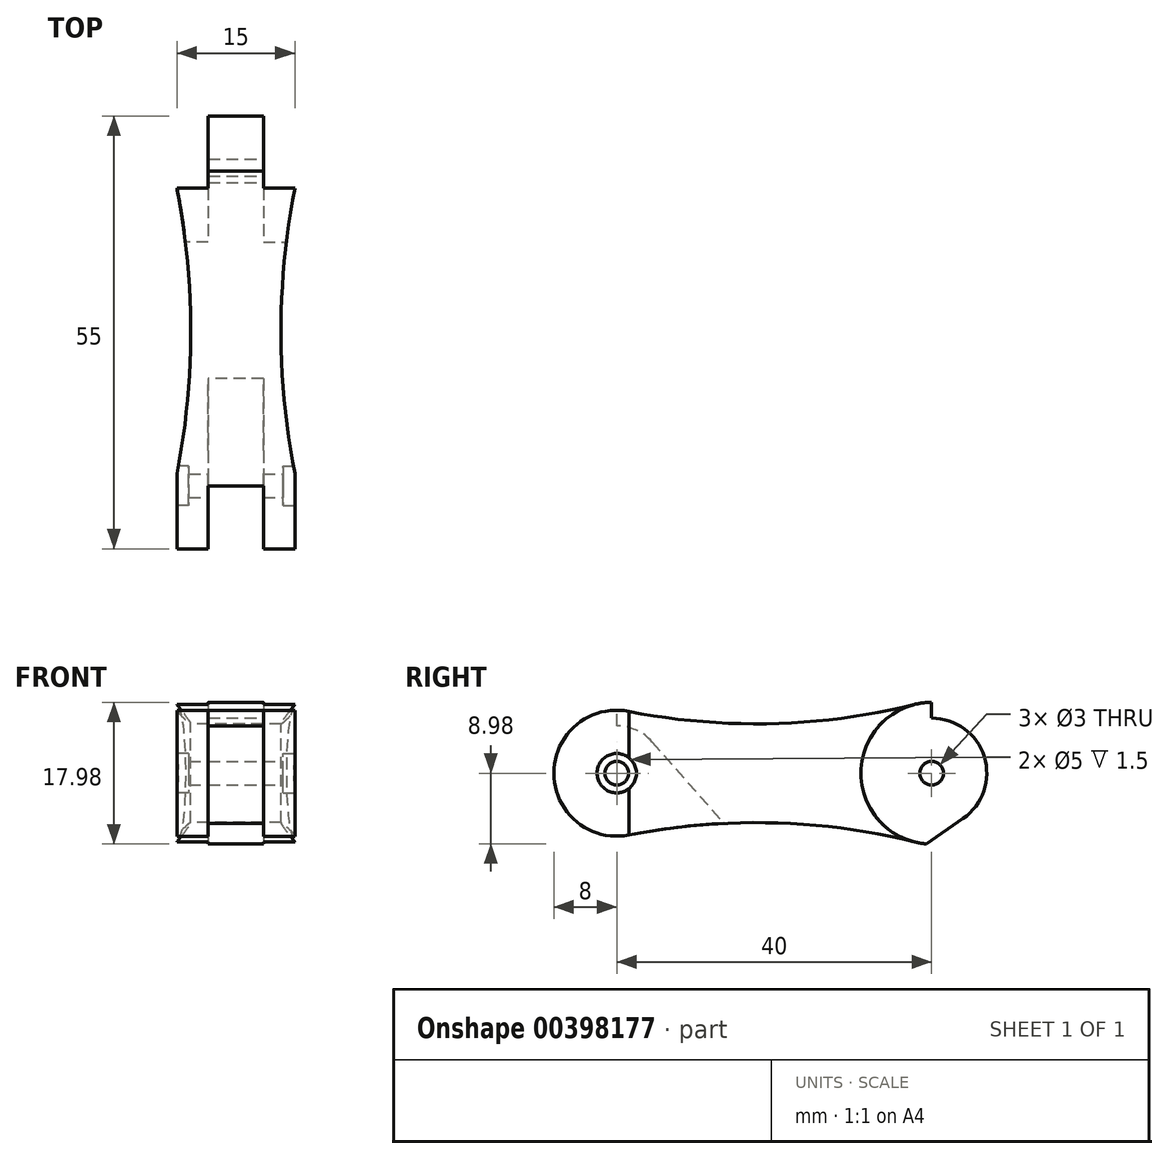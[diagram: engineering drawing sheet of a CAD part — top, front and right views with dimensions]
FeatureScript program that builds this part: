
annotation { "Feature Type Name" : "Feature", "Feature Type Description" : "" }
export const myFeature = defineFeature(function(context is Context, id is Id, definition is map)
    precondition{}
    {
        {
            var Q0;
            Q0=qCreatedBy(makeId("Right.planeOp"),FACE);
            var sketch = newSketch(context, id + "F0", { "sketchPlane" : qUnion([Q0])});
            skArc(sketch, "E0", {"start": v(1.54, 7.85) * mm, "mid": v(-8, 0) * mm, "end": v(1.54, -7.85) * mm});
            skLineSegment(sketch, "E1", {"start": v(-29.92, 0) * mm, "end": v(87.26, 0) * mm, "construction": true});
            skArc(sketch, "E2", {"start": v(37.83, -8.74) * mm, "mid": v(49, 0) * mm, "end": v(37.83, 8.74) * mm});
            skArc(sketch, "E3", {"start": v(1.54, 7.85) * mm, "mid": v(19.74, 6.3) * mm, "end": v(37.83, 8.74) * mm});
            skArc(sketch, "E4", {"start": v(37.83, -8.74) * mm, "mid": v(19.74, -6.3) * mm, "end": v(1.54, -7.85) * mm});
            skSolve(sketch);
        }
        {
            var Q0;
            Q0=qSketchRegion(id+"F0",true);
            extrude(context, id + "F1", {"entities" : qUnion([Q0]), "depth" : 4 * mm});
        }
        {
            var Q0;
            Q0=makeQuery(id+"F1.opExtrude","CAP_FACE",FACE,{"disambiguationData":[OSD([sQuery(id+"F0.wireOp",EDGE,"E0"),sQuery(id+"F0.wireOp",EDGE,"E2"),sQuery(id+"F0.wireOp",EDGE,"E3"),sQuery(id+"F0.wireOp",EDGE,"E4")])],"isStart":false});
            var sketch = newSketch(context, id + "F2", { "sketchPlane" : qUnion([Q0])});
            skArc(sketch, "E5.0", {"start": v(37.83, -8.74) * mm, "mid": v(49, 0) * mm, "end": v(37.83, 8.74) * mm});
            skLineSegment(sketch, "E6", {"start": v(0, 0) * mm, "end": v(34.9, 0) * mm, "construction": true});
            skArc(sketch, "E7.0", {"start": v(1.54, 7.85) * mm, "mid": v(19.74, 6.3) * mm, "end": v(37.83, 8.74) * mm});
            skArc(sketch, "E8.0", {"start": v(37.83, -8.74) * mm, "mid": v(25.82, -6.67) * mm, "end": v(13.62, -6.38) * mm});
            skArc(sketch, "E9.0", {"start": v(1.54, 7.85) * mm, "mid": v(0.78, 7.96) * mm, "end": v(0, 8) * mm});
            skArc(sketch, "E10", {"start": v(4.5, 3.97) * mm, "mid": v(2.47, 5.47) * mm, "end": v(0, 6) * mm});
            skLineSegment(sketch, "E11", {"start": v(0, 6) * mm, "end": v(0, 8) * mm});
            skLineSegment(sketch, "E12", {"start": v(4.5, 3.97) * mm, "end": v(13.62, -6.38) * mm});
            skPoint(sketch, "E13.orphan", {"position": v(1.54, -7.85) * mm});
            skSolve(sketch);
        }
        {
            var Q0;
            Q0=qSketchRegion(id+"F2",true);
            extrude(context, id + "F3", {"entities" : qUnion([Q0]), "operationType" : NewBodyOperationType.ADD, "depth" : 7 * mm});
        }
        {
            var Q0;
            Q0=makeQuery(id+"F3.opExtrude","CAP_FACE",FACE,{"disambiguationData":[OSD([sQuery(id+"F2.wireOp",EDGE,"3bf56276-6e63-42ee-98d8-77259c1c36c8.0"),sQuery(id+"F2.wireOp",EDGE,"bc38228c-ca1f-41e0-8e1d-5deb207440e8.0"),sQuery(id+"F2.wireOp",EDGE,"a1095cbb-552a-4b33-82fb-9fb0068e6b7f.0"),sQuery(id+"F2.wireOp",EDGE,"E5.0"),sQuery(id+"F2.wireOp",EDGE,"kkhRfJHV-auDH-NZtS-KPEK-8B2iLmtzf0xF"),sQuery(id+"F2.wireOp",EDGE,"MWx028tx-hoiO-j3L1-AWWv-dpKiWbue3HpV"),sQuery(id+"F2.wireOp",EDGE,"JRJ70NO1-7vJe-Li3z-EIXT-plhISmGAnEbH")])],"isStart":false});
            var sketch = newSketch(context, id + "F4", { "sketchPlane" : qUnion([Q0])});
            skArc(sketch, "E14.0", {"start": v(1.54, 7.85) * mm, "mid": v(19.74, 6.3) * mm, "end": v(37.83, 8.74) * mm});
            skArc(sketch, "E15.0", {"start": v(0, 8) * mm, "mid": v(-7.96, -0.78) * mm, "end": v(1.54, -7.85) * mm});
            skArc(sketch, "E16.0", {"start": v(1.54, 7.85) * mm, "mid": v(0.78, 7.96) * mm, "end": v(0, 8) * mm});
            skArc(sketch, "E17.0", {"start": v(13.62, -6.38) * mm, "mid": v(7.56, -6.9) * mm, "end": v(1.54, -7.85) * mm});
            skArc(sketch, "E18.0", {"start": v(37.83, -8.74) * mm, "mid": v(25.82, -6.67) * mm, "end": v(13.62, -6.38) * mm});
            skArc(sketch, "E19.0", {"start": v(37.83, -8.74) * mm, "mid": v(49, 0) * mm, "end": v(37.83, 8.74) * mm});
            skSolve(sketch);
        }
        {
            var Q0;
            Q0=qSketchRegion(id+"F4",true);
            extrude(context, id + "F5", {"entities" : qUnion([Q0]), "operationType" : NewBodyOperationType.ADD, "depth" : 4 * mm});
        }
        {
            var Q0;
            {var subQ0=sQuery(id+"F4.wireOp",EDGE,"E19.0");Q0=makeQuery(id+"F13.boolean.opBoolean","SPLIT",FACE,{"disambiguationData":[TD([makeQuery(id+"F1.opExtrude","SWEPT_FACE",FACE,{"disambiguationData":[OSD([sQuery(id+"F0.wireOp",EDGE,"E2")])]})])],"derivedFrom":makeQuery(id+"F5.opExtrude","CAP_FACE",FACE,{"disambiguationData":[OSD([sQuery(id+"F4.wireOp",EDGE,"E14.0"),sQuery(id+"F4.wireOp",EDGE,"E15.0"),sQuery(id+"F4.wireOp",EDGE,"E16.0"),sQuery(id+"F4.wireOp",EDGE,"E17.0"),sQuery(id+"F4.wireOp",EDGE,"E18.0"),subQ0])],"isStart":false})});}
            var sketch = newSketch(context, id + "F6", { "sketchPlane" : qUnion([Q0])});
            skCircle(sketch, "E20", {"center": v(40, 0) * mm, "radius": 9 * mm});
            skSolve(sketch);
        }
        {
            var Q0;
            Q0 = qSketchRegion(id + "F6", true);
            extrude(context, id + "F7", {"entities" : qUnion([Q0]), "operationType" : NewBodyOperationType.REMOVE, "oppositeDirection" : true, "depth" : 4 * mm});
        }
        {
            var Q0;
            Q0=makeQuery(id+"F1.opExtrude","CAP_FACE",FACE,{"disambiguationData":[OSD([sQuery(id+"F0.wireOp",EDGE,"E0"),sQuery(id+"F0.wireOp",EDGE,"E2"),sQuery(id+"F0.wireOp",EDGE,"E3"),sQuery(id+"F0.wireOp",EDGE,"E4")])],"isStart":true});
            var sketch = newSketch(context, id + "F8", { "sketchPlane" : qUnion([Q0])});
            skCircle(sketch, "E21", {"center": v(-40, 0) * mm, "radius": 9 * mm});
            skSolve(sketch);
        }
        {
            var Q0;
            Q0=qSketchRegion(id+"F8",true);
            extrude(context, id + "F9", {"entities" : qUnion([Q0]), "operationType" : NewBodyOperationType.REMOVE, "oppositeDirection" : true, "depth" : 4 * mm});
        }
        {
            var Q0;
            Q0=makeQuery(id+"F1.opExtrude","CAP_FACE",FACE,{"disambiguationData":[OSD([sQuery(id+"F0.wireOp",EDGE,"E0"),sQuery(id+"F0.wireOp",EDGE,"E2"),sQuery(id+"F0.wireOp",EDGE,"E3"),sQuery(id+"F0.wireOp",EDGE,"E4")])],"isStart":true});
            var sketch = newSketch(context, id + "F10", { "sketchPlane" : qUnion([Q0])});
            skCircle(sketch, "E22", {"center": v(0, 0) * mm, "radius": 2.5 * mm});
            skSolve(sketch);
        }
        {
            var Q0;
            Q0=qSketchRegion(id+"F10",true);
            extrude(context, id + "F11", {"entities" : qUnion([Q0]), "operationType" : NewBodyOperationType.REMOVE, "oppositeDirection" : true, "depth" : 1.5 * mm});
        }
        {
            var Q0;
            Q0=qCreatedBy(makeId("Top.planeOp"),FACE);
            var sketch = newSketch(context, id + "F12", { "sketchPlane" : qUnion([Q0])});
            skCircle(sketch, "E23", {"center": v(-92, 19.69) * mm, "radius": 93.77 * mm});
            skCircle(sketch, "E24", {"center": v(107, 19.69) * mm, "radius": 93.77 * mm});
            skSolve(sketch);
        }
        {
            var Q0;
            Q0=qSketchRegion(id+"F12",true);
            extrude(context, id + "F13", {"entities" : qUnion([Q0]), "operationType" : NewBodyOperationType.REMOVE, "endBound" : BoundingType.SYMMETRIC, "oppositeDirection" : true, "depth" : 25 * mm});
        }
        {
            var Q0;
            Q0=makeQuery(id+"F7.boolean.opBoolean","COPY",FACE,{"derivedFrom":makeQuery(id+"F7.opExtrude","CAP_FACE",FACE,{"disambiguationData":[OSD([sQuery(id+"F6.wireOp",EDGE,"E20")])],"isStart":false})});
            var sketch = newSketch(context, id + "F14", { "sketchPlane" : qUnion([Q0])});
            skCircle(sketch, "E25", {"center": v(40, 0) * mm, "radius": 1.5 * mm});
            skSolve(sketch);
        }
        {
            var Q0;
            Q0 = qSketchRegion(id + "F14", true);
            extrude(context, id + "F15", {"entities" : qUnion([Q0]), "operationType" : NewBodyOperationType.REMOVE, "endBound" : BoundingType.THROUGH_ALL, "oppositeDirection" : true, "depth" : 25 * mm});
        }
        {
            var Q0;
            Q0=makeQuery(id+"F5.opExtrude","CAP_FACE",FACE,{"disambiguationData":[OSD([sQuery(id+"F4.wireOp",EDGE,"E14.0"),sQuery(id+"F4.wireOp",EDGE,"E15.0"),sQuery(id+"F4.wireOp",EDGE,"E16.0"),sQuery(id+"F4.wireOp",EDGE,"E17.0"),sQuery(id+"F4.wireOp",EDGE,"E18.0"),sQuery(id+"F4.wireOp",EDGE,"E19.0")])],"isStart":false});
            var sketch = newSketch(context, id + "F16", { "sketchPlane" : qUnion([Q0])});
            skCircle(sketch, "E26", {"center": v(0, 0) * mm, "radius": 1.5 * mm});
            skSolve(sketch);
        }
        {
            var Q0;
            Q0 = qSketchRegion(id + "F16", true);
            extrude(context, id + "F17", {"entities" : qUnion([Q0]), "operationType" : NewBodyOperationType.REMOVE, "endBound" : BoundingType.THROUGH_ALL, "oppositeDirection" : true, "depth" : 25 * mm});
        }
        {
            var Q0;
            Q0=makeQuery(id+"F5.opExtrude","CAP_FACE",FACE,{"disambiguationData":[OSD([sQuery(id+"F4.wireOp",EDGE,"E14.0"),sQuery(id+"F4.wireOp",EDGE,"E15.0"),sQuery(id+"F4.wireOp",EDGE,"E16.0"),sQuery(id+"F4.wireOp",EDGE,"E17.0"),sQuery(id+"F4.wireOp",EDGE,"E18.0"),sQuery(id+"F4.wireOp",EDGE,"E19.0")])],"isStart":false});
            var sketch = newSketch(context, id + "F18", { "sketchPlane" : qUnion([Q0])});
            skCircle(sketch, "E27", {"center": v(0, 0) * mm, "radius": 2.5 * mm});
            skSolve(sketch);
        }
        {
            var Q0;
            Q0 = qSketchRegion(id + "F18", true);
            extrude(context, id + "F19", {"entities" : qUnion([Q0]), "operationType" : NewBodyOperationType.REMOVE, "oppositeDirection" : true, "depth" : 1.5 * mm});
        }
        {
            var Q0;
            Q0=makeQuery(id+"F7.boolean.opBoolean","COPY",FACE,{"derivedFrom":makeQuery(id+"F7.opExtrude","CAP_FACE",FACE,{"disambiguationData":[OSD([sQuery(id+"F6.wireOp",EDGE,"E20")])],"isStart":false})});
            var sketch = newSketch(context, id + "F20", { "sketchPlane" : qUnion([Q0])});
            skArc(sketch, "E28", {"start": v(44, -5.74) * mm, "mid": v(46.68, 2.1) * mm, "end": v(40, 7) * mm});
            skArc(sketch, "E29.0", {"start": v(39.36, -8.98) * mm, "mid": v(49, -0.32) * mm, "end": v(40, 9) * mm});
            skLineSegment(sketch, "E30", {"start": v(40, 7) * mm, "end": v(40, 9) * mm});
            skLineSegment(sketch, "E31", {"start": v(44, -5.74) * mm, "end": v(39.36, -8.98) * mm});
            skPoint(sketch, "E32.orphan", {"position": v(37.83, -8.74) * mm});
            skPoint(sketch, "E33.orphan", {"position": v(37.83, 8.74) * mm});
            skSolve(sketch);
        }
        {
            var Q0;
            Q0 = qSketchRegion(id + "F20", true);
            extrude(context, id + "F21", {"entities" : qUnion([Q0]), "operationType" : NewBodyOperationType.REMOVE, "endBound" : BoundingType.THROUGH_ALL, "oppositeDirection" : true, "depth" : 25 * mm});
        }
    });
